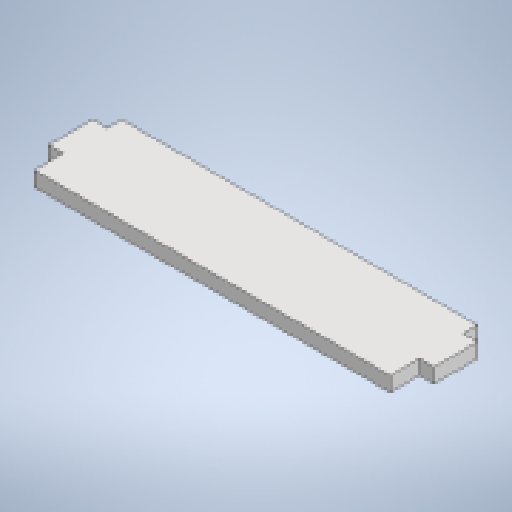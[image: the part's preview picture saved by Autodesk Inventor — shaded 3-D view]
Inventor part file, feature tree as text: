
AUTODESK INVENTOR PART (.ipt)
format: ipt  version: 2023 (Build 270158000, 158)  size: 159,744 bytes
history: native  units: mm
features: extrude x2, sketch x2
ambient origin geometry x8: Origin, YZ Plane, XZ Plane, XY Plane, X Axis, Y Axis, Z Axis, Center Point
bodies: Solid1 (feature_tree)
feature tree (4):
  extrude  "Extrusion1"  Depth=132.0mm
  extrude  "Extrusion2"  Depth=5.0mm
  sketch  "Sketch1"  dims[d0=5.0mm d1=132.0mm]
  sketch  "Sketch2"  dims[d2=30.0mm d3=0.0mm d4=5.0mm d5=15.0mm d6=15.0mm d7=5.0mm d8=0.0mm d9=10.0mm d10=0.0mm d11=5.0mm d12=5.0mm d13=5.0mm d14=10.0mm]
